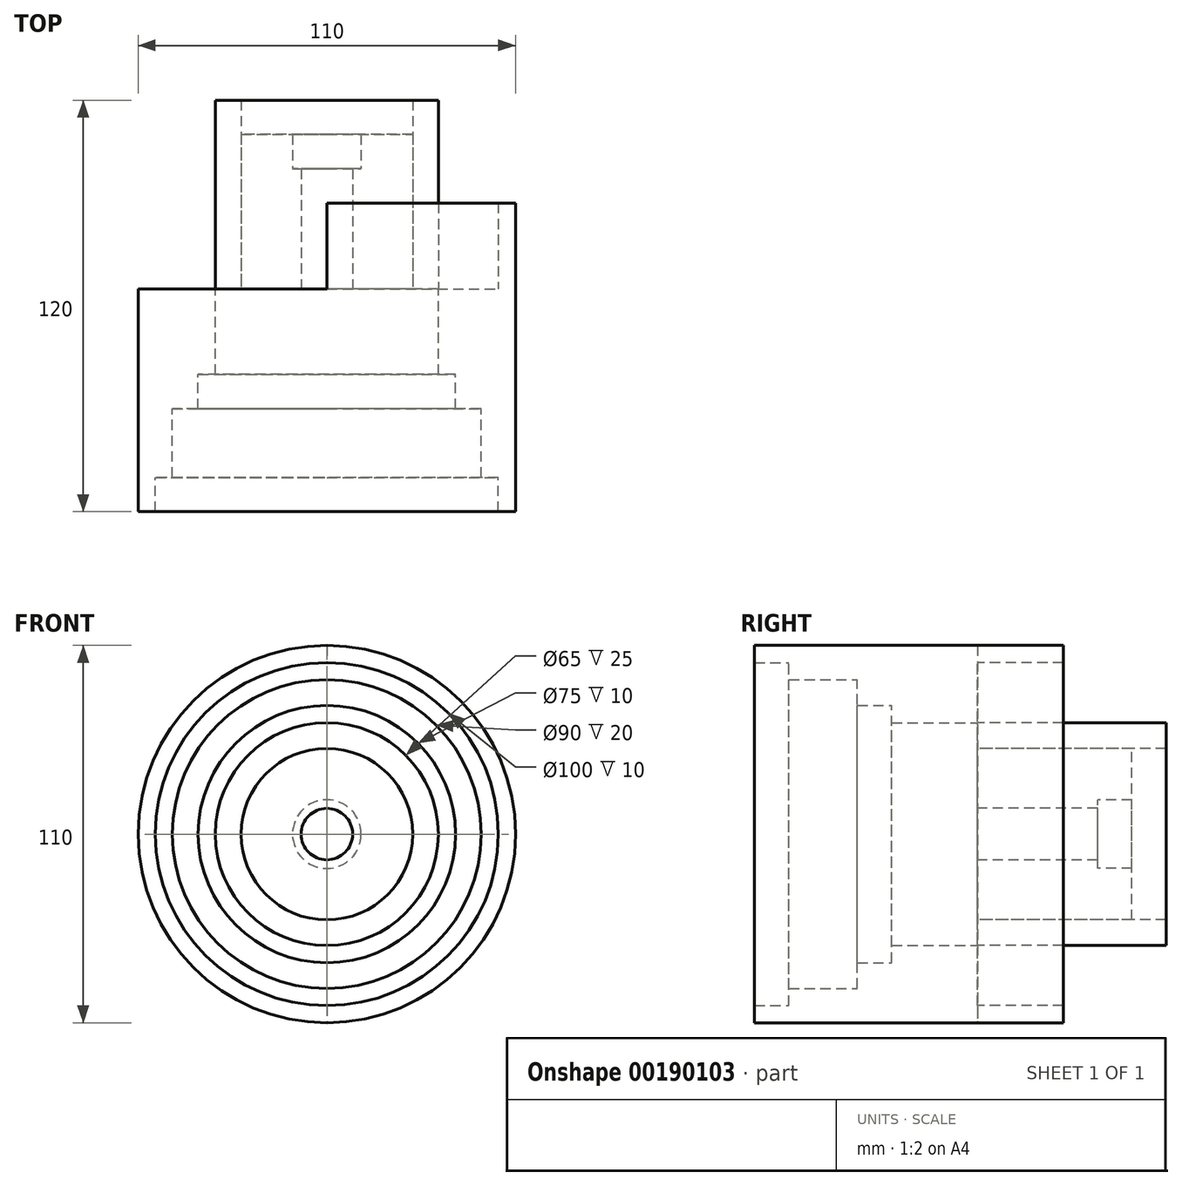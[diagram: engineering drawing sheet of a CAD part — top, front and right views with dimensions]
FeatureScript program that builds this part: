
annotation { "Feature Type Name" : "Feature", "Feature Type Description" : "" }
export const myFeature = defineFeature(function(context is Context, id is Id, definition is map)
    precondition{}
    {
        {
            var Q0;
            Q0=qCreatedBy(makeId("Front.planeOp"),FACE);
            var sketch = newSketch(context, id + "F0", { "sketchPlane" : qUnion([Q0])});
            skCircle(sketch, "E0", {"center": v(0, 0) * mm, "radius": 55 * mm});
            skCircle(sketch, "E1", {"center": v(0, 0) * mm, "radius": 50 * mm});
            skCircle(sketch, "E2", {"center": v(0, 0) * mm, "radius": 45 * mm});
            skCircle(sketch, "E3", {"center": v(0, 0) * mm, "radius": 37.5 * mm});
            skCircle(sketch, "E4", {"center": v(0, 0) * mm, "radius": 32.5 * mm});
            skCircle(sketch, "E5", {"center": v(0, 0) * mm, "radius": 25 * mm});
            skCircle(sketch, "E6", {"center": v(0, 0) * mm, "radius": 10 * mm});
            skCircle(sketch, "E7", {"center": v(0, 0) * mm, "radius": 7.5 * mm});
            skLineSegment(sketch, "E8", {"start": v(0, 55) * mm, "end": v(0, -55) * mm});
            skSolve(sketch);
        }
        {
            var Q0;
            Q0=makeQuery(id+"F0.imprint","IMPRINT",FACE,{"disambiguationData":[TD([[makeQuery(id+"F0.imprint","IMPRINT",EDGE,{"derivedFrom":sQuery(id+"F0.wireOp",EDGE,"E6")}),1.0]])]});
            var Q1;
            Q1=sQuery(id+"F0.wireOp",EDGE,"E6");
            var Q2;
            Q2=sQuery(id+"F0.wireOp",EDGE,"E7");
            extrude(context, id + "F1", {"entities" : qUnion([Q0]), "surfaceEntities" : qUnion([Q1, Q2]), "oppositeDirection" : true, "depth" : 35 * mm});
        }
        {
            var Q0;
            Q0=makeQuery(id+"F0.imprint","IMPRINT",FACE,{"disambiguationData":[TD([[makeQuery(id+"F0.imprint","IMPRINT",EDGE,{"derivedFrom":sQuery(id+"F0.wireOp",EDGE,"E5")}),1.0]])]});
            var Q1;
            Q1=sQuery(id+"F0.wireOp",EDGE,"E5");
            extrude(context, id + "F2", {"entities" : qUnion([Q0]), "operationType" : NewBodyOperationType.ADD, "surfaceEntities" : qUnion([Q1]), "oppositeDirection" : true, "depth" : 45 * mm});
        }
        {
            var Q0;
            Q0=makeQuery(id+"F0.imprint","IMPRINT",FACE,{"disambiguationData":[TD([[makeQuery(id+"F0.imprint","IMPRINT",EDGE,{"derivedFrom":sQuery(id+"F0.wireOp",EDGE,"E4")}),1.0]])]});
            var Q1;
            Q1=sQuery(id+"F0.wireOp",EDGE,"E4");
            extrude(context, id + "F3", {"entities" : qUnion([Q0]), "surfaceEntities" : qUnion([Q1]), "oppositeDirection" : true, "depth" : 55 * mm});
        }
        {
            var Q0;
            Q0=makeQuery(id+"F0.imprint","IMPRINT",FACE,{"disambiguationData":[TD([[makeQuery(id+"F0.imprint","IMPRINT",EDGE,{"derivedFrom":sQuery(id+"F0.wireOp",EDGE,"E3")}),1.0]])]});
            var Q1;
            Q1=sQuery(id+"F0.wireOp",EDGE,"E3");
            extrude(context, id + "F4", {"entities" : qUnion([Q0]), "surfaceEntities" : qUnion([Q1]), "depth" : 25 * mm});
        }
        {
            var Q0;
            Q0=makeQuery(id+"F0.imprint","IMPRINT",FACE,{"disambiguationData":[TD([[makeQuery(id+"F0.imprint","IMPRINT",EDGE,{"derivedFrom":sQuery(id+"F0.wireOp",EDGE,"E2")}),1.0]])]});
            var Q1;
            Q1=sQuery(id+"F0.wireOp",EDGE,"E2");
            extrude(context, id + "F5", {"entities" : qUnion([Q0]), "operationType" : NewBodyOperationType.ADD, "surfaceEntities" : qUnion([Q1]), "depth" : 35 * mm});
        }
        {
            var Q0;
            Q0=makeQuery(id+"F0.imprint","IMPRINT",FACE,{"disambiguationData":[TD([[makeQuery(id+"F0.imprint","IMPRINT",EDGE,{"derivedFrom":sQuery(id+"F0.wireOp",EDGE,"E1")}),1.0]])]});
            var Q1;
            Q1=sQuery(id+"F0.wireOp",EDGE,"E1");
            extrude(context, id + "F6", {"entities" : qUnion([Q0]), "operationType" : NewBodyOperationType.ADD, "surfaceEntities" : qUnion([Q1]), "depth" : 55 * mm});
        }
        {
            var Q0;
            Q0=makeQuery(id+"F0.imprint","IMPRINT",FACE,{"disambiguationData":[TD([[makeQuery(id+"F0.imprint","IMPRINT",EDGE,{"derivedFrom":sQuery(id+"F0.wireOp",EDGE,"E0")}),1.0]])]});
            var Q1;
            Q1=sQuery(id+"F0.wireOp",EDGE,"E0");
            extrude(context, id + "F7", {"entities" : qUnion([Q0]), "operationType" : NewBodyOperationType.ADD, "surfaceEntities" : qUnion([Q1]), "depth" : 65 * mm});
        }
        {
            var Q0;
            {var subQ0=sQuery(id+"F0.wireOp",EDGE,"E8");var subQ1=sQuery(id+"F0.wireOp",EDGE,"E0");var subQ2=makeQuery(id+"F0.imprint","INTERSECT",VERTEX,{"disambiguationData":[OD(0.0)],"derivedFrom":[subQ1,subQ0]});Q0=makeQuery(id+"F0.imprint","IMPRINT",FACE,{"disambiguationData":[TD([[makeQuery(id+"F0.imprint","IMPRINT",EDGE,{"disambiguationData":[TD([[subQ2,-1.0]])],"derivedFrom":subQ1}),1.0]])]});}
            extrude(context, id + "F8", {"entities" : qUnion([Q0]), "operationType" : NewBodyOperationType.ADD, "oppositeDirection" : true, "depth" : 25 * mm});
        }
    });
